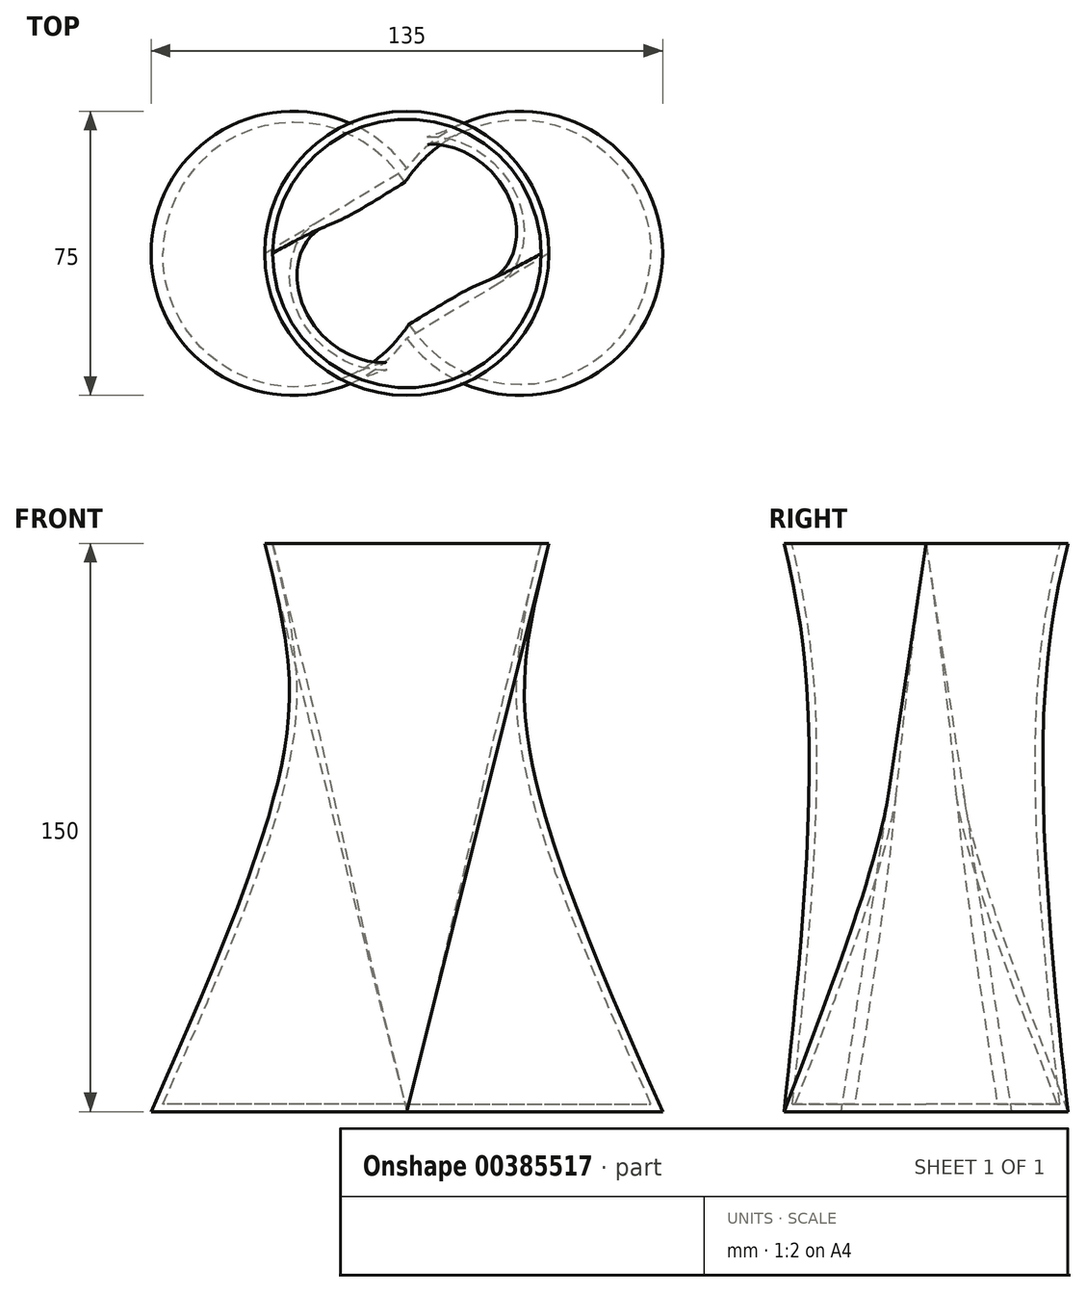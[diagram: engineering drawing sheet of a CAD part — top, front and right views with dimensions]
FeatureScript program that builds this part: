
annotation { "Feature Type Name" : "Feature", "Feature Type Description" : "" }
export const myFeature = defineFeature(function(context is Context, id is Id, definition is map)
    precondition{}
    {
        {
            var Q0;
            Q0=qCreatedBy(makeId("Top.planeOp"),FACE);
            var sketch = newSketch(context, id + "F0", { "sketchPlane" : qUnion([Q0])});
            skArc(sketch, "E0", {"start": v(0, 37.5) * mm, "mid": v(-26.52, 26.52) * mm, "end": v(-37.5, 0) * mm});
            skArc(sketch, "E1", {"start": v(37.5, 0) * mm, "mid": v(26.52, 26.52) * mm, "end": v(0, 37.5) * mm});
            skArc(sketch, "E2", {"start": v(0, -37.5) * mm, "mid": v(26.52, -26.52) * mm, "end": v(37.5, 0) * mm});
            skArc(sketch, "E3", {"start": v(-37.5, 0) * mm, "mid": v(-26.52, -26.52) * mm, "end": v(0, -37.5) * mm});
            skSolve(sketch);
        }
        {
            var Q0;
            Q0=qCreatedBy(makeId("Top.planeOp"),FACE);
            cPlane(context, id + "F1", {"entities" : qUnion([Q0]), "cplaneType" : CPlaneType.OFFSET, "offset" : 150 * mm, "oppositeDirection" : true, "width" : 150 * mm, "height" : 150 * mm});
        }
        {
            var Q0;
            Q0=qCreatedBy(id+"F1.planeOp",FACE);
            var sketch = newSketch(context, id + "F2", { "sketchPlane" : qUnion([Q0])});
            skArc(sketch, "E4", {"start": v(0, 22.5) * mm, "mid": v(-41.86, 35.58) * mm, "end": v(-67.5, 0) * mm});
            skArc(sketch, "E5.MirrorC", {"start": v(0, 22.5) * mm, "mid": v(41.86, 35.58) * mm, "end": v(67.5, 0) * mm});
            skArc(sketch, "E6", {"start": v(-67.5, 0) * mm, "mid": v(-41.86, -35.58) * mm, "end": v(0, -22.5) * mm});
            skArc(sketch, "E7", {"start": v(67.5, 0) * mm, "mid": v(41.86, -35.58) * mm, "end": v(0, -22.5) * mm});
            skSolve(sketch);
        }
        {
            var Q0;
            Q0=makeQuery(id+"F0.imprint","IMPRINT",FACE,{"disambiguationData":[TD([[makeQuery(id+"F0.imprint","IMPRINT",EDGE,{"derivedFrom":sQuery(id+"F0.wireOp",EDGE,"E0")}),1.0]])]});
            var Q1;
            Q1=makeQuery(id+"F2.imprint","IMPRINT",FACE,{"disambiguationData":[TD([[makeQuery(id+"F2.imprint","IMPRINT",EDGE,{"derivedFrom":sQuery(id+"F2.wireOp",EDGE,"E4")}),1.0]])]});
            var Q2;
            Q2=sQuery(id+"F2.wireOp",VERTEX,"E6.end");
            var Q3;
            Q3=sQuery(id+"F0.wireOp",VERTEX,"E2.end");
            loft(context, id + "F3", {"sheetProfilesArray" : [{ "sheetProfileEntities" : qUnion([Q0]) }, { "sheetProfileEntities" : qUnion([Q1]) }], "matchConnections" : true, "connections" : [{ "connectionEntities" : qUnion([Q2, Q3]), "connectionEdgeQueries" : qUnion([]), "connectionEdgeParameters" : [] }]});
        }
        {
            var Q0;
            Q0=makeQuery(id+"F3.opLoft","CAP_FACE",FACE,{"disambiguationData":[OSD([makeQuery(id+"F0.imprint","IMPRINT",FACE,{"disambiguationData":[TD([[makeQuery(id+"F0.imprint","IMPRINT",EDGE,{"derivedFrom":sQuery(id+"F0.wireOp",EDGE,"E0")}),1.0]])]})])],"isStart":true});
            shell(context, id + "F4", {"entities" : qUnion([Q0]), "thickness" : 2 * mm});
        }
    });
